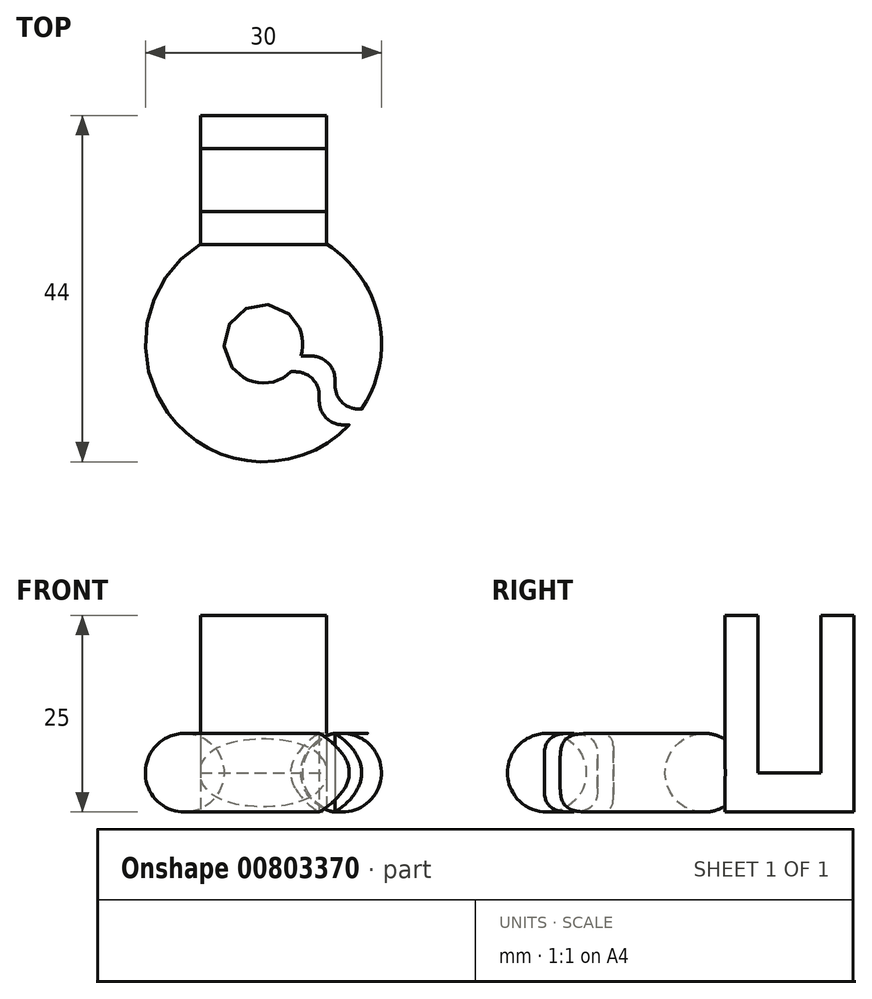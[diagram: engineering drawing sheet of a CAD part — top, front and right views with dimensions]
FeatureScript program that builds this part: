
annotation { "Feature Type Name" : "Feature", "Feature Type Description" : "" }
export const myFeature = defineFeature(function(context is Context, id is Id, definition is map)
    precondition{}
    {
        {
            var Q0;
            Q0=qCreatedBy(makeId("Top.planeOp"),FACE);
            var sketch = newSketch(context, id + "F0", { "sketchPlane" : qUnion([Q0])});
            skLineSegment(sketch, "E0.bottom", {"start": v(-8, 4.2) * mm, "end": v(8, 4.2) * mm});
            skLineSegment(sketch, "E0.top", {"start": v(-8, 0) * mm, "end": v(8, 0) * mm});
            skLineSegment(sketch, "E0.left", {"start": v(-8, 4.2) * mm, "end": v(-8, 0) * mm});
            skLineSegment(sketch, "E0.right", {"start": v(8, 4.2) * mm, "end": v(8, 0) * mm});
            skSolve(sketch);
        }
        {
            var Q0;
            Q0 = qSketchRegion(id + "F0", true);
            extrude(context, id + "F1", {"entities" : qUnion([Q0]), "depth" : 25 * mm, "offsetDistance" : 25 * mm});
        }
        {
            var Q0;
            Q0=qCreatedBy(makeId("Top.planeOp"),FACE);
            var sketch = newSketch(context, id + "F2", { "sketchPlane" : qUnion([Q0])});
            skLineSegment(sketch, "E1.bottom", {"start": v(-8, 4.2) * mm, "end": v(8, 4.2) * mm});
            skLineSegment(sketch, "E1.top", {"start": v(-8, 12.2) * mm, "end": v(8, 12.2) * mm});
            skLineSegment(sketch, "E1.left", {"start": v(-8, 4.2) * mm, "end": v(-8, 12.2) * mm});
            skLineSegment(sketch, "E1.right", {"start": v(8, 4.2) * mm, "end": v(8, 12.2) * mm});
            skSolve(sketch);
        }
        {
            var Q0;
            Q0 = qSketchRegion(id + "F2", true);
            extrude(context, id + "F3", {"entities" : qUnion([Q0]), "operationType" : NewBodyOperationType.ADD, "depth" : 5 * mm, "offsetDistance" : 25 * mm});
        }
        {
            var Q0;
            Q0=qCreatedBy(makeId("Top.planeOp"),FACE);
            var sketch = newSketch(context, id + "F4", { "sketchPlane" : qUnion([Q0])});
            skLineSegment(sketch, "E2.bottom", {"start": v(-8, 12.2) * mm, "end": v(8, 12.2) * mm});
            skLineSegment(sketch, "E2.top", {"start": v(-8, 16.4) * mm, "end": v(8, 16.4) * mm});
            skLineSegment(sketch, "E2.left", {"start": v(-8, 12.2) * mm, "end": v(-8, 16.4) * mm});
            skLineSegment(sketch, "E2.right", {"start": v(8, 12.2) * mm, "end": v(8, 16.4) * mm});
            skSolve(sketch);
        }
        {
            var Q0;
            Q0 = qSketchRegion(id + "F4", true);
            extrude(context, id + "F5", {"entities" : qUnion([Q0]), "operationType" : NewBodyOperationType.ADD, "depth" : 25 * mm, "offsetDistance" : 25 * mm});
        }
        {
            var Q0;
            Q0=qCreatedBy(makeId("Right.planeOp"),FACE);
            var sketch = newSketch(context, id + "F6", { "sketchPlane" : qUnion([Q0])});
            skCircle(sketch, "E3", {"center": v(-2.6, 5) * mm, "radius": 5 * mm});
            skLineSegment(sketch, "E4", {"start": v(-12.6, 15.9) * mm, "end": v(-12.6, -11.11) * mm, "construction": true});
            skLineSegment(sketch, "E5", {"start": v(2.4, 13.8) * mm, "end": v(2.4, -13.01) * mm, "construction": true});
            skSolve(sketch);
        }
        {
            var Q0;
            Q0 = qSketchRegion(id + "F6", true);
            var Q1;
            Q1=sQuery(id+"F6.wireOp",EDGE,"E4");
            revolve(context, id + "F7", {"operationType" : NewBodyOperationType.ADD, "surfaceOperationType" : NewSurfaceOperationType.NEW, "entities" : qUnion([Q0]), "axis" : qUnion([Q1]), "revolveType" : RevolveType.FULL});
        }
        {
            var Q0;
            Q0=qCreatedBy(makeId("Top.planeOp"),FACE);
            var sketch = newSketch(context, id + "F8", { "sketchPlane" : qUnion([Q0])});
            skLineSegment(sketch, "E6", {"start": v(3.28, -14.16) * mm, "end": v(9.1, -14.16) * mm});
            skLineSegment(sketch, "E7", {"start": v(9.1, -14.16) * mm, "end": v(9.1, -20.9) * mm});
            skLineSegment(sketch, "E8", {"start": v(9.1, -20.9) * mm, "end": v(13.26, -20.9) * mm});
            skPoint(sketch, "E9", {"position": v(9.1, -18.39) * mm});
            skLineSegment(sketch, "E10", {"start": v(3.31, -16.16) * mm, "end": v(7.1, -16.16) * mm});
            skLineSegment(sketch, "E11", {"start": v(7.1, -16.16) * mm, "end": v(7.1, -22.9) * mm});
            skLineSegment(sketch, "E12", {"start": v(7.1, -22.9) * mm, "end": v(13.22, -22.9) * mm});
            skLineSegment(sketch, "E13", {"start": v(3.28, -14.16) * mm, "end": v(3.31, -16.16) * mm});
            skLineSegment(sketch, "E14", {"start": v(13.22, -22.9) * mm, "end": v(13.26, -20.9) * mm});
            skSolve(sketch);
        }
        {
            var Q0;
            Q0 = qSketchRegion(id + "F8", true);
            extrude(context, id + "F9", {"entities" : qUnion([Q0]), "operationType" : NewBodyOperationType.REMOVE, "depth" : 10 * mm, "offsetDistance" : 25 * mm});
        }
        {
            var Q0;
            Q0=makeQuery(id+"F9.boolean.opBoolean","COPY",EDGE,{"derivedFrom":makeQuery(id+"F9.opExtrude","SWEPT_EDGE",EDGE,{"disambiguationData":[OSD([sQuery(id+"F8.wireOp",EDGE,"E10"),sQuery(id+"F8.wireOp",EDGE,"E11")])]})});
            var Q1;
            Q1=makeQuery(id+"F9.boolean.opBoolean","COPY",EDGE,{"derivedFrom":makeQuery(id+"F9.opExtrude","SWEPT_EDGE",EDGE,{"disambiguationData":[OSD([sQuery(id+"F8.wireOp",EDGE,"E7"),sQuery(id+"F8.wireOp",EDGE,"E8")])]})});
            fillet(context, id + "F10", {"entities" : qUnion([Q0, Q1]), "radius" : 3 * mm, "tangentPropagation" : true, "allowEdgeOverflow" : false});
        }
        {
            var Q0;
            Q0=makeQuery(id+"F9.boolean.opBoolean","COPY",EDGE,{"derivedFrom":makeQuery(id+"F9.opExtrude","SWEPT_EDGE",EDGE,{"disambiguationData":[OSD([sQuery(id+"F8.wireOp",EDGE,"E6"),sQuery(id+"F8.wireOp",EDGE,"E7")])]})});
            var Q1;
            Q1=makeQuery(id+"F9.boolean.opBoolean","COPY",EDGE,{"derivedFrom":makeQuery(id+"F9.opExtrude","SWEPT_EDGE",EDGE,{"disambiguationData":[OSD([sQuery(id+"F8.wireOp",EDGE,"E11"),sQuery(id+"F8.wireOp",EDGE,"E12")])]})});
            fillet(context, id + "F11", {"entities" : qUnion([Q0, Q1]), "radius" : 3 * mm, "tangentPropagation" : true, "allowEdgeOverflow" : false});
        }
    });
